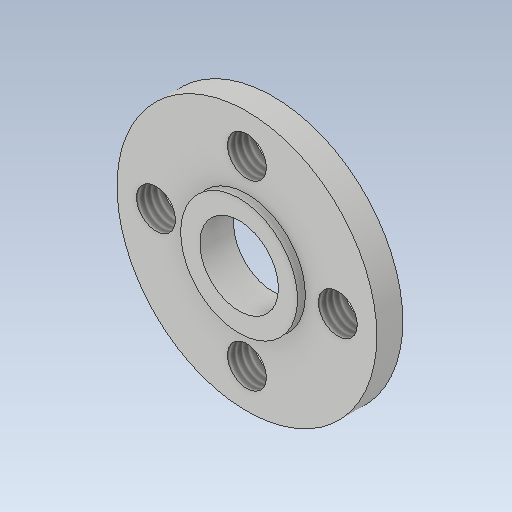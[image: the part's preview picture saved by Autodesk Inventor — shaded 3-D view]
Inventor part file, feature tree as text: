
AUTODESK INVENTOR PART (.ipt)
format: ipt  version: 2020.1 (Build 241239000, 239)  size: 146,944 bytes
history: native  units: mm
features: extrude x4, thread x4, sketch x4
ambient origin geometry x8: Origin, YZ Plane, XZ Plane, XY Plane, X Axis, Y Axis, Z Axis, Center Point
bodies: Solid1 (feature_tree)
feature tree (12):
  extrude  "Extrusion1"  Depth=2.0mm TaperAngle=0.0deg
  extrude  "Extrusion2"  Depth=0.6mm TaperAngle=0.0deg
  extrude  "Extrusion4"  Depth=2.5mm TaperAngle=0.0deg
  extrude  "Extrusion5"  Depth=10.0mm
  thread  "Thread1"  [1 undecoded]
  thread  "Thread2"  [1 undecoded]
  thread  "Thread3"  [1 undecoded]
  thread  "Thread4"  [1 undecoded]
  sketch  "Sketch1"  dims[d0=20.0mm d1=2.0mm d2=0.0mm]
  sketch  "Sketch2"  dims[d3=9.0mm d4=0.6mm d5=0.0mm]
  sketch  "Sketch4"  dims[d9=6.05mm d10=2.5mm d11=0.0mm]
  sketch  "Sketch5"  dims[d12=7.0mm d13=3.0mm d14=40.0mm d16=360.0deg d18=2.5mm d19=0.0mm d20=10.0mm d21=0.0mm d22=10.0mm d23=0.0mm d24=10.0mm d25=0.0mm d26=10.0mm d27=0.0mm]
note: 4 required parameter values undecoded (feature->parameter linkage not recoverable at this tier; creation-order binding heuristic only, values carry confidence <= 0.55)
